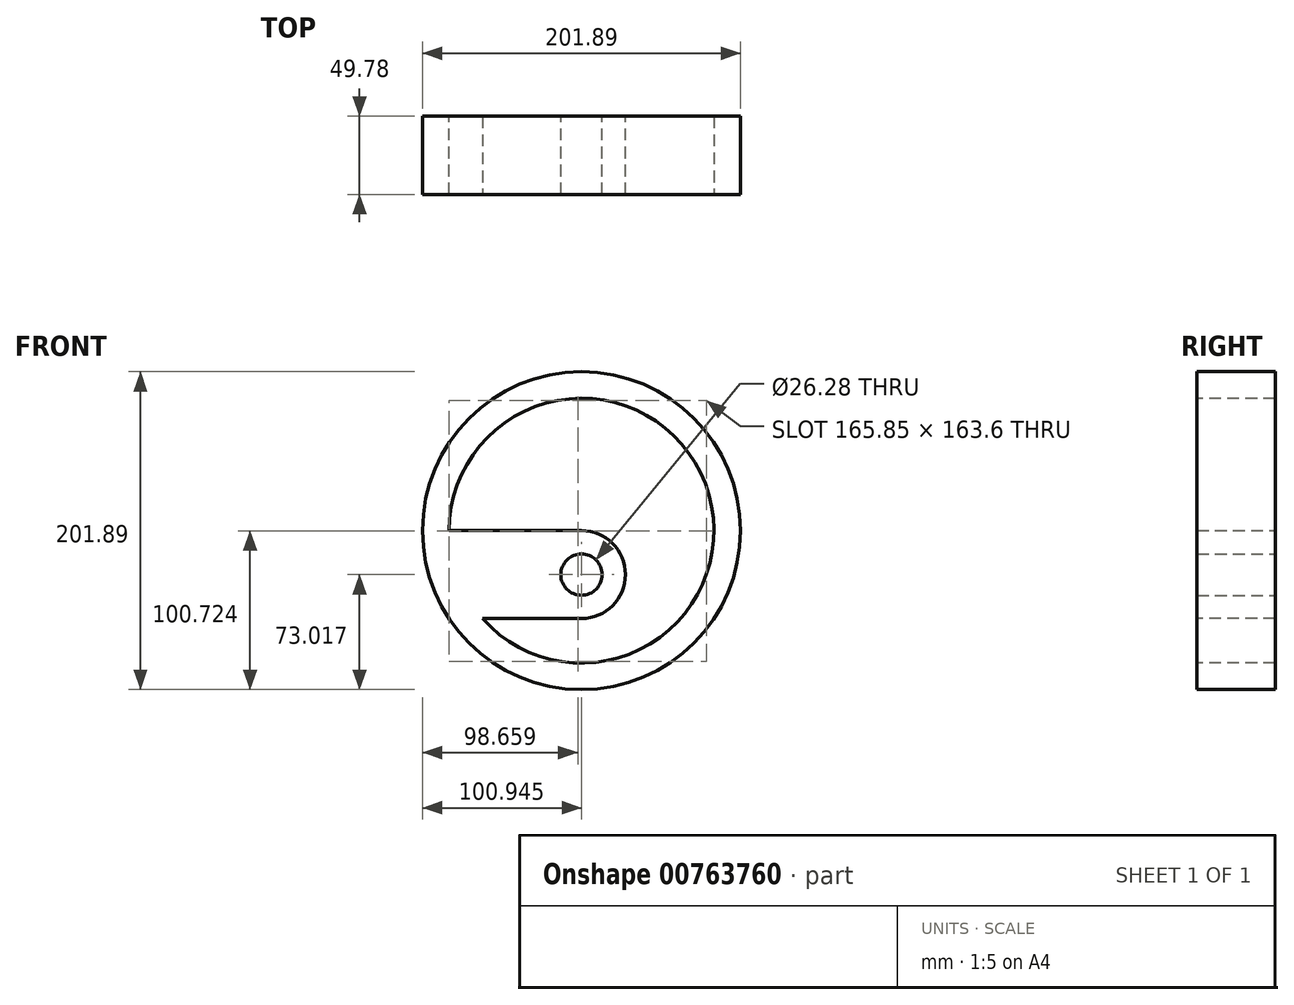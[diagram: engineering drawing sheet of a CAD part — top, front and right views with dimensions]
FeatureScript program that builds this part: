
annotation { "Feature Type Name" : "Feature", "Feature Type Description" : "" }
export const myFeature = defineFeature(function(context is Context, id is Id, definition is map)
    precondition{}
    {
        {
            var Q0;
            Q0=qCreatedBy(makeId("Front.planeOp"),FACE);
            var sketch = newSketch(context, id + "F0", { "sketchPlane" : qUnion([Q0])});
            skLineSegment(sketch, "E0.bottom", {"start": v(-58.2, 34.8) * mm, "end": v(25.89, 34.8) * mm});
            skLineSegment(sketch, "E0.top", {"start": v(-58.2, -21.05) * mm, "end": v(25.89, -21.05) * mm});
            skLineSegment(sketch, "E0.left", {"start": v(-58.2, 34.8) * mm, "end": v(-58.2, -21.05) * mm});
            skArc(sketch, "E1", {"start": v(25.89, -21.05) * mm, "mid": v(53.81, 6.88) * mm, "end": v(25.89, 34.8) * mm});
            skCircle(sketch, "E2", {"center": v(25.89, 6.88) * mm, "radius": 13.14 * mm});
            skSolve(sketch);
        }
        {
            var Q0;
            Q0=makeQuery(id+"F0.imprint","IMPRINT",FACE,{"disambiguationData":[TD([[makeQuery(id+"F0.imprint","IMPRINT",EDGE,{"derivedFrom":sQuery(id+"F0.wireOp",EDGE,"E0.bottom")}),-1.0]])]});
            extrude(context, id + "F1", {"entities" : qUnion([Q0]), "depth" : 49.78 * mm, "offsetDistance" : 25.4 * mm});
        }
        {
            var Q0;
            Q0=makeQuery(id+"F1.opExtrude","SWEPT_FACE",FACE,{"disambiguationData":[OSD([sQuery(id+"F0.wireOp",EDGE,"E0.left")])]});
            var Q1;
            Q1=makeQuery(id+"F1.opExtrude","SWEPT_EDGE",EDGE,{"disambiguationData":[OSD([sQuery(id+"F0.wireOp",EDGE,"E0.bottom"),sQuery(id+"F0.wireOp",EDGE,"E1")])]});
            revolve(context, id + "F2", {"operationType" : NewBodyOperationType.ADD, "surfaceOperationType" : NewSurfaceOperationType.NEW, "entities" : qUnion([Q0]), "axis" : qUnion([Q1]), "revolveType" : RevolveType.FULL});
        }
    });
